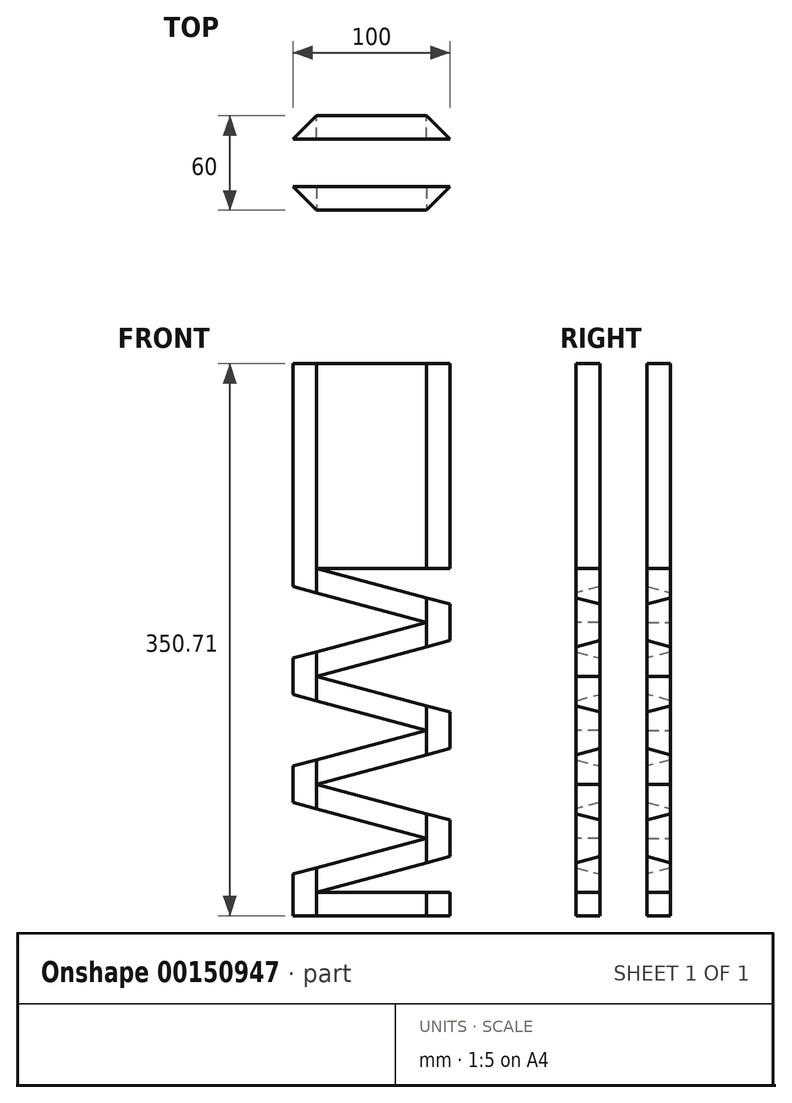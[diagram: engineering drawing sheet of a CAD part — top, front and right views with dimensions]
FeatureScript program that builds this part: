
annotation { "Feature Type Name" : "Feature", "Feature Type Description" : "" }
export const myFeature = defineFeature(function(context is Context, id is Id, definition is map)
    precondition{}
    {
        {
            var Q0;
            Q0=qCreatedBy(makeId("Front.planeOp"),FACE);
            var sketch = newSketch(context, id + "F0", { "sketchPlane" : qUnion([Q0])});
            skLineSegment(sketch, "E0.bottom", {"start": v(50, -65) * mm, "end": v(-50, -65) * mm});
            skLineSegment(sketch, "E0.top", {"start": v(50, 65) * mm, "end": v(-50, 65) * mm});
            skLineSegment(sketch, "E0.left", {"start": v(50, -65) * mm, "end": v(50, 65) * mm});
            skLineSegment(sketch, "E0.right", {"start": v(-50, -65) * mm, "end": v(-50, 65) * mm});
            skPoint(sketch, "E0.middle", {"position": v(0, 0) * mm});
            skLineSegment(sketch, "E1", {"start": v(-35, -65) * mm, "end": v(50, -87.78) * mm});
            skLineSegment(sketch, "E2", {"start": v(50, -87.78) * mm, "end": v(50, -110.8) * mm});
            skLineSegment(sketch, "E3", {"start": v(50, -110.8) * mm, "end": v(-35, -133.57) * mm});
            skLineSegment(sketch, "E4", {"start": v(-50, -65) * mm, "end": v(-50, -76.5) * mm});
            skLineSegment(sketch, "E5", {"start": v(-50, -76.5) * mm, "end": v(35, -99.29) * mm});
            skLineSegment(sketch, "E6", {"start": v(35, -99.29) * mm, "end": v(-50, -122.06) * mm});
            skLineSegment(sketch, "E7", {"start": v(-50, -65) * mm, "end": v(-50, -315) * mm, "construction": true});
            skLineSegment(sketch, "E8", {"start": v(50, -65) * mm, "end": v(50, -315) * mm, "construction": true});
            skLineSegment(sketch, "E9", {"start": v(-35, -133.57) * mm, "end": v(50, -156.35) * mm});
            skLineSegment(sketch, "E10", {"start": v(50, -156.35) * mm, "end": v(50, -179.37) * mm});
            skLineSegment(sketch, "E11", {"start": v(50, -179.37) * mm, "end": v(-35, -202.14) * mm});
            skLineSegment(sketch, "E12", {"start": v(-35, -202.14) * mm, "end": v(50, -224.92) * mm});
            skLineSegment(sketch, "E13", {"start": v(50, -224.92) * mm, "end": v(50, -247.94) * mm});
            skLineSegment(sketch, "E14", {"start": v(50, -247.94) * mm, "end": v(-35, -270.71) * mm});
            skLineSegment(sketch, "E15", {"start": v(-50, -122.06) * mm, "end": v(-50, -145.08) * mm});
            skLineSegment(sketch, "E16", {"start": v(35, -167.86) * mm, "end": v(-50, -190.63) * mm});
            skLineSegment(sketch, "E17", {"start": v(-50, -190.63) * mm, "end": v(-50, -213.65) * mm});
            skLineSegment(sketch, "E18", {"start": v(-50, -213.65) * mm, "end": v(35, -236.43) * mm});
            skLineSegment(sketch, "E19", {"start": v(35, -236.43) * mm, "end": v(-50, -259.2) * mm});
            skLineSegment(sketch, "E20", {"start": v(-50, -259.2) * mm, "end": v(-50, -285.71) * mm});
            skLineSegment(sketch, "E21", {"start": v(-50, -285.71) * mm, "end": v(50, -285.71) * mm});
            skLineSegment(sketch, "E22", {"start": v(50, -285.71) * mm, "end": v(50, -270.71) * mm});
            skLineSegment(sketch, "E23", {"start": v(50, -270.71) * mm, "end": v(-35, -270.71) * mm});
            skLineSegment(sketch, "E24", {"start": v(35, -167.86) * mm, "end": v(-50, -145.08) * mm});
            skSolve(sketch);
        }
        {
            var Q0;
            {var subQ0=sQuery(id+"F0.wireOp",EDGE,"E1");Q0=makeQuery(id+"F0.imprint","IMPRINT",FACE,{"disambiguationData":[TD([[makeQuery(id+"F0.imprint","IMPRINT",EDGE,{"derivedFrom":subQ0}),-1.0]])]});}
            var Q1;
            Q1=makeQuery(id+"F0.imprint","IMPRINT",FACE,{"disambiguationData":[TD([[makeQuery(id+"F0.imprint","IMPRINT",EDGE,{"derivedFrom":sQuery(id+"F0.wireOp",EDGE,"E0.top")}),1.0]])]});
            extrude(context, id + "F1", {"entities" : qUnion([Q0, Q1]), "depth" : 15 * mm});
        }
        {
            var Q0;
            Q0=makeQuery(id+"F1.opExtrude","SWEPT_FACE",FACE,{"disambiguationData":[OSD([sQuery(id+"F0.wireOp",EDGE,"E0.top")])]});
            var sketch = newSketch(context, id + "F2", { "sketchPlane" : qUnion([Q0])});
            skLineSegment(sketch, "E25", {"start": v(-50, -15) * mm, "end": v(-35, 0) * mm});
            skLineSegment(sketch, "E26", {"start": v(35, 0) * mm, "end": v(50, -15) * mm});
            skSolve(sketch);
        }
        {
            var Q0;
            {var subQ0=sQuery(id+"F2.wireOp",EDGE,"E25");Q0=makeQuery(id+"F2.imprint","IMPRINT",FACE,{"disambiguationData":[TD([[makeQuery(id+"F2.imprint","IMPRINT",EDGE,{"derivedFrom":subQ0}),1.0]])]});}
            var Q1;
            {var subQ0=sQuery(id+"F2.wireOp",EDGE,"E26");Q1=makeQuery(id+"F2.imprint","IMPRINT",FACE,{"disambiguationData":[TD([[makeQuery(id+"F2.imprint","IMPRINT",EDGE,{"derivedFrom":subQ0}),1.0]])]});}
            extrude(context, id + "F3", {"entities" : qUnion([Q0, Q1]), "operationType" : NewBodyOperationType.REMOVE, "endBound" : BoundingType.THROUGH_ALL, "oppositeDirection" : true, "depth" : 25 * mm});
        }
        {
            var Q0;
            Q0=makeQuery(id+"F1.opExtrude","SWEPT_BODY",BODY,{"disambiguationData":[OSD([sQuery(id+"F0.wireOp",EDGE,"E0.bottom"),sQuery(id+"F0.wireOp",EDGE,"E0.top"),sQuery(id+"F0.wireOp",EDGE,"E0.left"),sQuery(id+"F0.wireOp",EDGE,"E0.right"),sQuery(id+"F0.wireOp",EDGE,"E1"),sQuery(id+"F0.wireOp",EDGE,"E2"),sQuery(id+"F0.wireOp",EDGE,"E3"),sQuery(id+"F0.wireOp",EDGE,"E4"),sQuery(id+"F0.wireOp",EDGE,"E5"),sQuery(id+"F0.wireOp",EDGE,"E6"),sQuery(id+"F0.wireOp",EDGE,"E9"),sQuery(id+"F0.wireOp",EDGE,"E10"),sQuery(id+"F0.wireOp",EDGE,"E11"),sQuery(id+"F0.wireOp",EDGE,"E12"),sQuery(id+"F0.wireOp",EDGE,"E13"),sQuery(id+"F0.wireOp",EDGE,"E14"),sQuery(id+"F0.wireOp",EDGE,"E15"),sQuery(id+"F0.wireOp",EDGE,"E16"),sQuery(id+"F0.wireOp",EDGE,"E17"),sQuery(id+"F0.wireOp",EDGE,"E18"),sQuery(id+"F0.wireOp",EDGE,"E19"),sQuery(id+"F0.wireOp",EDGE,"E20"),sQuery(id+"F0.wireOp",EDGE,"E21"),sQuery(id+"F0.wireOp",EDGE,"E22"),sQuery(id+"F0.wireOp",EDGE,"E23"),sQuery(id+"F0.wireOp",EDGE,"E24")])]});
            var Q1;
            Q1=makeQuery(id+"F1.opExtrude","CAP_FACE",FACE,{"disambiguationData":[OSD([sQuery(id+"F0.wireOp",EDGE,"E0.bottom"),sQuery(id+"F0.wireOp",EDGE,"E0.top"),sQuery(id+"F0.wireOp",EDGE,"E0.left"),sQuery(id+"F0.wireOp",EDGE,"E0.right"),sQuery(id+"F0.wireOp",EDGE,"E1"),sQuery(id+"F0.wireOp",EDGE,"E2"),sQuery(id+"F0.wireOp",EDGE,"E3"),sQuery(id+"F0.wireOp",EDGE,"E4"),sQuery(id+"F0.wireOp",EDGE,"E5"),sQuery(id+"F0.wireOp",EDGE,"E6"),sQuery(id+"F0.wireOp",EDGE,"E9"),sQuery(id+"F0.wireOp",EDGE,"E10"),sQuery(id+"F0.wireOp",EDGE,"E11"),sQuery(id+"F0.wireOp",EDGE,"E12"),sQuery(id+"F0.wireOp",EDGE,"E13"),sQuery(id+"F0.wireOp",EDGE,"E14"),sQuery(id+"F0.wireOp",EDGE,"E15"),sQuery(id+"F0.wireOp",EDGE,"E16"),sQuery(id+"F0.wireOp",EDGE,"E17"),sQuery(id+"F0.wireOp",EDGE,"E18"),sQuery(id+"F0.wireOp",EDGE,"E19"),sQuery(id+"F0.wireOp",EDGE,"E20"),sQuery(id+"F0.wireOp",EDGE,"E21"),sQuery(id+"F0.wireOp",EDGE,"E22"),sQuery(id+"F0.wireOp",EDGE,"E23"),sQuery(id+"F0.wireOp",EDGE,"E24")])],"isStart":false});
            mirror(context, id + "F4", {"entities" : qUnion([Q0]), "mirrorPlane" : qUnion([Q1])});
        }
        {
            var Q0;
            Q0=makeQuery(id+"F4.opPattern","COPY",BODY,{"derivedFrom":makeQuery(id+"F1.opExtrude","SWEPT_BODY",BODY,{"disambiguationData":[OSD([sQuery(id+"F0.wireOp",EDGE,"E0.bottom"),sQuery(id+"F0.wireOp",EDGE,"E0.top"),sQuery(id+"F0.wireOp",EDGE,"E0.left"),sQuery(id+"F0.wireOp",EDGE,"E0.right"),sQuery(id+"F0.wireOp",EDGE,"E1"),sQuery(id+"F0.wireOp",EDGE,"E2"),sQuery(id+"F0.wireOp",EDGE,"E3"),sQuery(id+"F0.wireOp",EDGE,"E4"),sQuery(id+"F0.wireOp",EDGE,"E5"),sQuery(id+"F0.wireOp",EDGE,"E6"),sQuery(id+"F0.wireOp",EDGE,"E9"),sQuery(id+"F0.wireOp",EDGE,"E10"),sQuery(id+"F0.wireOp",EDGE,"E11"),sQuery(id+"F0.wireOp",EDGE,"E12"),sQuery(id+"F0.wireOp",EDGE,"E13"),sQuery(id+"F0.wireOp",EDGE,"E14"),sQuery(id+"F0.wireOp",EDGE,"E15"),sQuery(id+"F0.wireOp",EDGE,"E16"),sQuery(id+"F0.wireOp",EDGE,"E17"),sQuery(id+"F0.wireOp",EDGE,"E18"),sQuery(id+"F0.wireOp",EDGE,"E19"),sQuery(id+"F0.wireOp",EDGE,"E20"),sQuery(id+"F0.wireOp",EDGE,"E21"),sQuery(id+"F0.wireOp",EDGE,"E22"),sQuery(id+"F0.wireOp",EDGE,"E23"),sQuery(id+"F0.wireOp",EDGE,"E24")])]}),"instanceName":"1"});
            transform(context, id + "F5", {"entities" : qUnion([Q0]), "transformType" : TransformType.TRANSLATION_3D, "dx" : 0 * mm, "dy" : -30 * mm, "dz" : 0 * mm, "makeCopy" : false});
        }
    });
